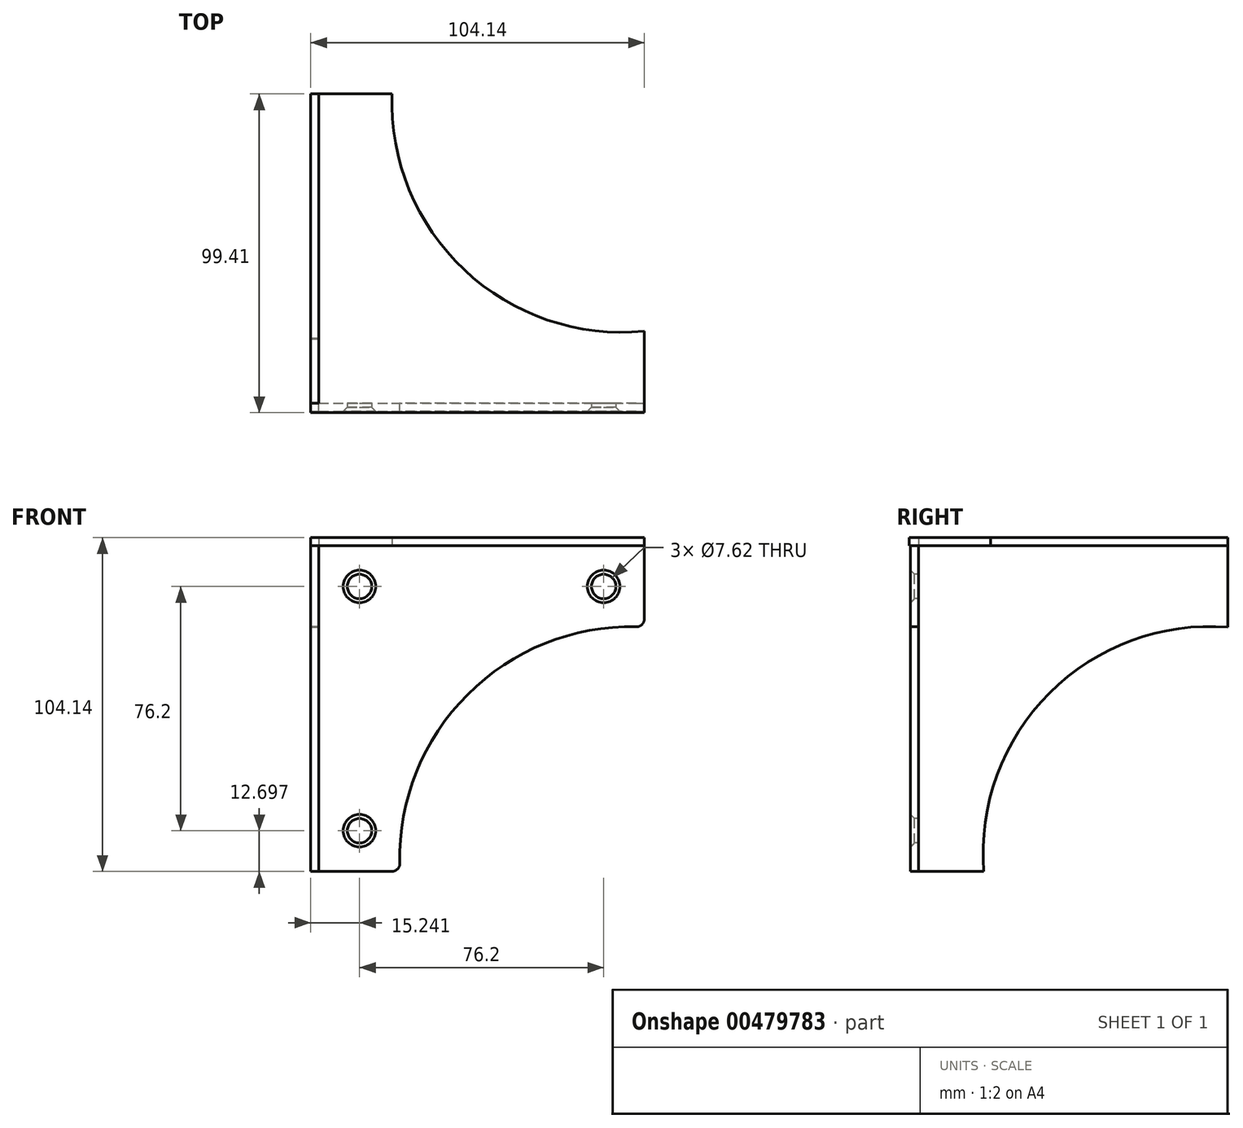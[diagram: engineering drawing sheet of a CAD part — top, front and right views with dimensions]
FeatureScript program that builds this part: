
annotation { "Feature Type Name" : "Feature", "Feature Type Description" : "" }
export const myFeature = defineFeature(function(context is Context, id is Id, definition is map)
    precondition{}
    {
        {
            var Q0;
            Q0=qCreatedBy(makeId("Front.planeOp"),FACE);
            var sketch = newSketch(context, id + "F0", { "sketchPlane" : qUnion([Q0])});
            skLineSegment(sketch, "E0", {"start": v(-57.85, 46.92) * mm, "end": v(-57.85, -54.68) * mm});
            skLineSegment(sketch, "E1", {"start": v(-57.85, 46.92) * mm, "end": v(43.75, 46.92) * mm});
            skLineSegment(sketch, "E2", {"start": v(43.75, 46.92) * mm, "end": v(43.75, 21.52) * mm});
            skLineSegment(sketch, "E3", {"start": v(-57.85, -54.68) * mm, "end": v(-32.45, -54.68) * mm});
            skArc(sketch, "E4", {"start": v(43.75, 21.52) * mm, "mid": v(-11.44, 0.5) * mm, "end": v(-32.45, -54.68) * mm});
            skSolve(sketch);
        }
        {
            var Q0;
            Q0=makeQuery(id+"F0.imprint","IMPRINT",FACE,{"disambiguationData":[TD([[makeQuery(id+"F0.imprint","IMPRINT",EDGE,{"derivedFrom":sQuery(id+"F0.wireOp",EDGE,"E0")}),1.0]])]});
            extrude(context, id + "F1", {"entities" : qUnion([Q0]), "depth" : 2.54 * mm});
        }
        {
            var Q0;
            Q0=makeQuery(id+"F1.opExtrude","SWEPT_EDGE",EDGE,{"disambiguationData":[OSD([sQuery(id+"F0.wireOp",EDGE,"E2"),sQuery(id+"F0.wireOp",EDGE,"E4")])]});
            fillet(context, id + "F2", {"entities" : qUnion([Q0]), "radius" : 2.54 * mm, "tangentPropagation" : true, "allowEdgeOverflow" : false});
        }
        {
            var Q0;
            Q0=makeQuery(id+"F1.opExtrude","SWEPT_EDGE",EDGE,{"disambiguationData":[OSD([sQuery(id+"F0.wireOp",EDGE,"E3"),sQuery(id+"F0.wireOp",EDGE,"E4")])]});
            fillet(context, id + "F3", {"entities" : qUnion([Q0]), "radius" : 2.54 * mm, "tangentPropagation" : true, "allowEdgeOverflow" : false});
        }
        {
            var Q0;
            Q0=makeQuery(id+"F1.opExtrude","SWEPT_FACE",FACE,{"disambiguationData":[OSD([sQuery(id+"F0.wireOp",EDGE,"E0")])]});
            var sketch = newSketch(context, id + "F4", { "sketchPlane" : qUnion([Q0])});
            skLineSegment(sketch, "E5", {"start": v(2.54, 46.92) * mm, "end": v(-96.52, 46.92) * mm});
            skLineSegment(sketch, "E6", {"start": v(-96.52, 46.92) * mm, "end": v(-96.52, 21.52) * mm});
            skLineSegment(sketch, "E7", {"start": v(2.54, -54.68) * mm, "end": v(-20.32, -54.68) * mm});
            skArc(sketch, "E8", {"start": v(-20.32, -54.68) * mm, "mid": v(-40.86, 0.98) * mm, "end": v(-96.52, 21.52) * mm});
            skSolve(sketch);
        }
        {
            var Q0;
            {var subQ3=sQuery(id+"F4.wireOp",EDGE,"E6");Q0=makeQuery(id+"F4.imprint","IMPRINT",FACE,{"disambiguationData":[TD([[makeQuery(id+"F4.imprint","IMPRINT",EDGE,{"derivedFrom":subQ3}),1.0]])]});}
            extrude(context, id + "F5", {"entities" : qUnion([Q0]), "depth" : 2.54 * mm});
        }
        {
            var Q0;
            Q0=makeQuery(id+"F1.opExtrude","SWEPT_FACE",FACE,{"disambiguationData":[OSD([sQuery(id+"F0.wireOp",EDGE,"E0")])]});
            extrude(context, id + "F6", {"entities" : qUnion([Q0]), "depth" : 2.54 * mm});
        }
        {
            var Q0;
            Q0=makeQuery(id+"F5.opExtrude","SWEPT_FACE",FACE,{"disambiguationData":[OSD([sQuery(id+"F4.wireOp",EDGE,"E5")])]});
            var sketch = newSketch(context, id + "F7", { "sketchPlane" : qUnion([Q0])});
            skLineSegment(sketch, "E9", {"start": v(-60.39, 96.52) * mm, "end": v(-60.39, -2.89) * mm});
            skLineSegment(sketch, "E10", {"start": v(-60.39, -2.89) * mm, "end": v(43.7, -2.89) * mm});
            skLineSegment(sketch, "E11", {"start": v(43.7, -2.89) * mm, "end": v(43.7, 22.51) * mm});
            skLineSegment(sketch, "E12", {"start": v(-60.39, 96.52) * mm, "end": v(-34.99, 96.52) * mm});
            skArc(sketch, "E13", {"start": v(-34.99, 96.52) * mm, "mid": v(-12.44, 41.65) * mm, "end": v(43.7, 22.51) * mm});
            skSolve(sketch);
        }
        {
            var Q0;
            {var subQ4=sQuery(id+"F7.wireOp",EDGE,"E10");Q0=makeQuery(id+"F7.imprint","IMPRINT",FACE,{"disambiguationData":[TD([[makeQuery(id+"F7.imprint","IMPRINT",EDGE,{"derivedFrom":subQ4}),1.0]])]});}
            extrude(context, id + "F8", {"entities" : qUnion([Q0]), "depth" : 2.54 * mm});
        }
        {
            var Q0;
            Q0=makeQuery(id+"F8.opExtrude","SWEPT_FACE",FACE,{"disambiguationData":[OSD([sQuery(id+"F4.wireOp",EDGE,"E5")])]});
            extrude(context, id + "F9", {"entities" : qUnion([Q0]), "depth" : 2.54 * mm});
        }
        {
            var Q0;
            Q0=makeQuery(id+"F1.opExtrude","CAP_FACE",FACE,{"disambiguationData":[OSD([sQuery(id+"F0.wireOp",EDGE,"E0"),sQuery(id+"F0.wireOp",EDGE,"E1"),sQuery(id+"F0.wireOp",EDGE,"E2"),sQuery(id+"F0.wireOp",EDGE,"E3"),sQuery(id+"F0.wireOp",EDGE,"E4")])],"isStart":false});
            var sketch = newSketch(context, id + "F10", { "sketchPlane" : qUnion([Q0])});
            skLineSegment(sketch, "E14", {"start": v(-57.85, 46.92) * mm, "end": v(-45.15, 46.92) * mm});
            skLineSegment(sketch, "E15", {"start": v(-45.15, 46.92) * mm, "end": v(-45.15, 34.22) * mm});
            skLineSegment(sketch, "E16", {"start": v(-45.15, 34.22) * mm, "end": v(-57.85, 34.22) * mm});
            skLineSegment(sketch, "E17", {"start": v(43.75, 34.22) * mm, "end": v(31.05, 34.22) * mm});
            skPoint(sketch, "E17.startSnap0", {"position": v(43.75, 35.54) * mm});
            skLineSegment(sketch, "E18", {"start": v(-45.15, -54.68) * mm, "end": v(-45.15, -41.98) * mm});
            skPoint(sketch, "E18.startSnap0", {"position": v(-46.47, -54.68) * mm});
            skCircle(sketch, "E19", {"center": v(-45.15, 34.22) * mm, "radius": 3.81 * mm});
            skCircle(sketch, "E20", {"center": v(-45.15, -41.98) * mm, "radius": 3.81 * mm});
            skCircle(sketch, "E21", {"center": v(31.05, 34.22) * mm, "radius": 3.81 * mm});
            skSolve(sketch);
        }
        {
            var Q0;
            Q0=sQuery(id+"F10.wireOp",VERTEX,"E16.start");
            var Q1;
            Q1=sQuery(id+"F10.wireOp",VERTEX,"E17.end");
            var Q2;
            Q2=sQuery(id+"F10.wireOp",VERTEX,"E20.center");
            var Q3;
            Q3=makeQuery(id+"F1.opExtrude","SWEPT_BODY",BODY,{"disambiguationData":[OSD([sQuery(id+"F0.wireOp",EDGE,"E0"),sQuery(id+"F0.wireOp",EDGE,"E1"),sQuery(id+"F0.wireOp",EDGE,"E2"),sQuery(id+"F0.wireOp",EDGE,"E3"),sQuery(id+"F0.wireOp",EDGE,"E4")])]});
            hole(context, id + "F11", {"style" : HoleStyle.C_SINK, "endStyle" : HoleEndStyle.BLIND, "holeDiameter" : 7.62 * mm, "cSinkDiameter" : 10.16 * mm, "cSinkAngle" : 90 * degree, "holeDepth" : 25.4 * mm, "isTappedThrough" : true, "tappedDepth" : 12.7 * mm, "tapClearance" : 3, "startFromSketch" : true, "locations" : qUnion([Q0, Q1, Q2]), "scope" : qUnion([Q3])});
        }
    });
